SOLIDWORKS PART (.sldprt)
format: sldprt  version: not decoded by parser v0  size: 327,680 bytes
history: native  units: mm
features: sketch x12, extrude x6, cut_extrude x6, fillet x2, material x1, chamfer x1 (+13 scaffold rows collapsed)
feature tree (41):
  scaffold x13  (default folders/planes/origin — collapsed)
  material  "Material <not specified>"
  sketch  "Sketch1"  dims[D1=15.0mm D2=8.0mm D3=31.0mm]
  extrude  "Boss-Extrude1"  Depth=1mm
  sketch  "Sketch2"  dims[c1.D1=~8.508106mm c1.D2=0.0mm c2.D1=7.5mm c2.D2=7.5mm c2.D3=~7.408036mm c3.D1=5.5mm c3.D2=7.5mm c3.D3=7.5mm]
  extrude  "Boss-Extrude2"  Depth=6mm
  fillet  "Fillet1"  Radius=2.75mm
  fillet  "Fillet2"  Radius=4mm
  sketch  "Sketch3"  dims[D1=3.0mm D2=3.0mm D3=6.0mm]
  extrude  "Boss-Extrude3"  Depth=15mm
  sketch  "Sketch4"  dims[c1.D1=1.0mm c1.D2=2.0mm c2.D1=1.0mm c2.D3=1.0mm c2.D4=10.5mm]
  extrude  "Boss-Extrude4"  Depth=6mm
  sketch  "Sketch5"  dims[D1=~0.962837mm]
  cut_extrude  "Cut-Extrude1"  Depth=6mm
  sketch  "Sketch6"
  cut_extrude  "Cut-Extrude2"  Depth=6mm
  sketch  "Sketch7"  dims[D1=3.0mm]
  cut_extrude  "Cut-Extrude3"  [1 undecoded]
  sketch  "Sketch8"  dims[D1=~3.119045mm]
  extrude  "Boss-Extrude5"  Depth=1mm
  sketch  "Sketch9"  dims[D1=~3.119045mm]
  extrude  "Boss-Extrude6"  [1 undecoded]
  sketch  "Sketch10"  dims[D2=~11.419444mm D1=0.0mm]
  cut_extrude  "Cut-Extrude4"  [1 undecoded]
  sketch  "Sketch11"  dims[D2=1.0mm D3=3.0mm D4=3.0mm D1=0.0mm]
  cut_extrude  "Cut-Extrude5"  [1 undecoded]
  chamfer  "Chamfer1"  Distance=1mm Angle=45deg
  sketch  "Sketch12"  dims[D1=3.1mm D2=3.1mm]
  cut_extrude  "Cut-Extrude6"  [1 undecoded]
decode coverage: 21 of 27 modeling features carry decoded parameters
note: ~ marks probable driven/reference dimensions
note: 5 parameter values undecoded
summary: no parameter record found for 5 features
note: suppression state not decoded; provenance and decode notes live in map.json
